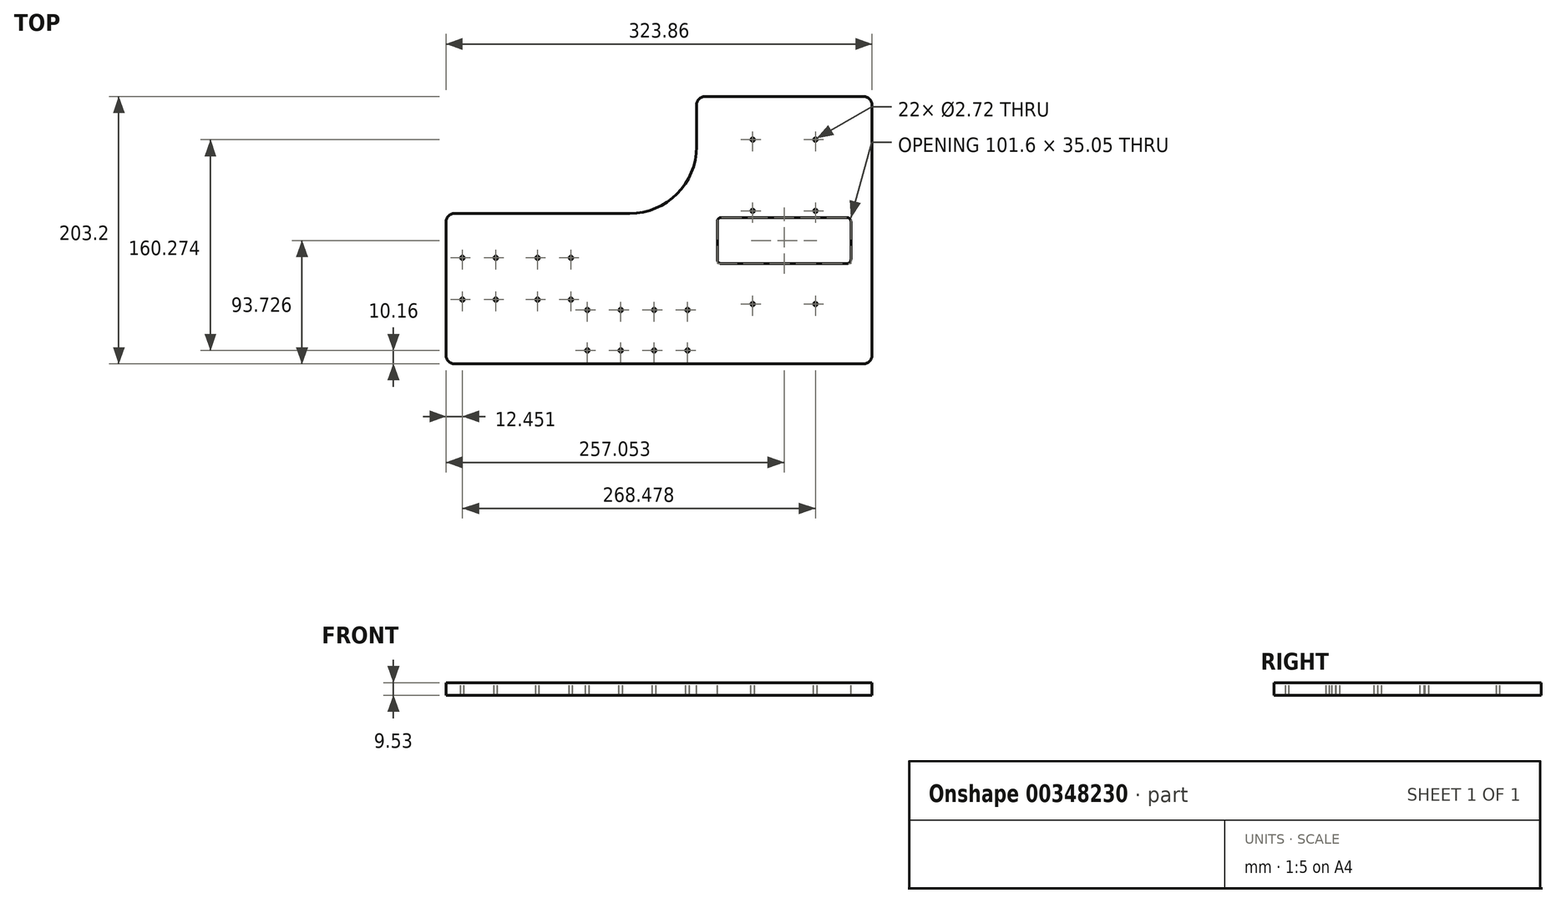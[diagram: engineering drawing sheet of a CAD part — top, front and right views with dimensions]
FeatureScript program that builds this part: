
annotation { "Feature Type Name" : "Feature", "Feature Type Description" : "" }
export const myFeature = defineFeature(function(context is Context, id is Id, definition is map)
    precondition{}
    {
        {
            var Q0;
            Q0=qCreatedBy(makeId("Top.planeOp"),FACE);
            var sketch = newSketch(context, id + "F0", { "sketchPlane" : qUnion([Q0])});
            skLineSegment(sketch, "E0", {"start": v(161.92, 95.25) * mm, "end": v(161.93, -95.25) * mm});
            skLineSegment(sketch, "E1", {"start": v(155.57, -101.6) * mm, "end": v(-155.58, -101.6) * mm});
            skLineSegment(sketch, "E2", {"start": v(-161.92, -95.25) * mm, "end": v(-161.92, 6.35) * mm});
            skLineSegment(sketch, "E3", {"start": v(-155.58, 12.7) * mm, "end": v(-22.22, 12.7) * mm});
            skLineSegment(sketch, "E4", {"start": v(28.58, 63.5) * mm, "end": v(28.58, 95.25) * mm});
            skLineSegment(sketch, "E5", {"start": v(34.93, 101.6) * mm, "end": v(155.57, 101.6) * mm});
            skPoint(sketch, "E6", {"position": v(0, -101.6) * mm});
            skPoint(sketch, "E7", {"position": v(161.92, 0) * mm});
            skPoint(sketch, "E8.visualSharp", {"position": v(28.58, 12.7) * mm});
            skArc(sketch, "E8.filletArc", {"start": v(-22.22, 12.7) * mm, "mid": v(13.7, 27.58) * mm, "end": v(28.58, 63.5) * mm});
            skPoint(sketch, "E9.visualSharp", {"position": v(161.93, -101.6) * mm});
            skArc(sketch, "E9.filletArc", {"start": v(155.57, -101.6) * mm, "mid": v(160.07, -99.74) * mm, "end": v(161.92, -95.25) * mm});
            skPoint(sketch, "E10.visualSharp", {"position": v(-161.92, -101.6) * mm});
            skArc(sketch, "E10.filletArc", {"start": v(-161.93, -95.25) * mm, "mid": v(-160.07, -99.74) * mm, "end": v(-155.58, -101.6) * mm});
            skPoint(sketch, "E11.visualSharp", {"position": v(-161.92, 12.7) * mm});
            skArc(sketch, "E11.filletArc", {"start": v(-155.58, 12.7) * mm, "mid": v(-160.07, 10.84) * mm, "end": v(-161.93, 6.35) * mm});
            skPoint(sketch, "E12.visualSharp", {"position": v(28.58, 101.6) * mm});
            skArc(sketch, "E12.filletArc", {"start": v(34.93, 101.6) * mm, "mid": v(30.43, 99.74) * mm, "end": v(28.58, 95.25) * mm});
            skPoint(sketch, "E13.visualSharp", {"position": v(161.92, 101.6) * mm});
            skArc(sketch, "E13.filletArc", {"start": v(161.92, 95.25) * mm, "mid": v(160.07, 99.74) * mm, "end": v(155.57, 101.6) * mm});
            skLineSegment(sketch, "E14.bottom", {"start": v(142.87, 9.65) * mm, "end": v(47.37, 9.65) * mm});
            skLineSegment(sketch, "E14.top", {"start": v(142.88, -25.4) * mm, "end": v(47.37, -25.4) * mm});
            skLineSegment(sketch, "E14.left", {"start": v(145.92, 6.6) * mm, "end": v(145.92, -22.35) * mm});
            skLineSegment(sketch, "E14.right", {"start": v(44.32, 6.6) * mm, "end": v(44.32, -22.35) * mm});
            skPoint(sketch, "E15.visualSharp", {"position": v(145.92, -25.4) * mm});
            skArc(sketch, "E15.filletArc", {"start": v(142.88, -25.4) * mm, "mid": v(145.03, -24.5) * mm, "end": v(145.92, -22.35) * mm});
            skPoint(sketch, "E16.visualSharp", {"position": v(44.32, -25.4) * mm});
            skArc(sketch, "E16.filletArc", {"start": v(44.32, -22.35) * mm, "mid": v(45.22, -24.5) * mm, "end": v(47.37, -25.4) * mm});
            skPoint(sketch, "E17.visualSharp", {"position": v(44.32, 9.65) * mm});
            skArc(sketch, "E17.filletArc", {"start": v(47.37, 9.65) * mm, "mid": v(45.22, 8.76) * mm, "end": v(44.32, 6.6) * mm});
            skPoint(sketch, "E18.visualSharp", {"position": v(145.92, 9.65) * mm});
            skArc(sketch, "E18.filletArc", {"start": v(145.92, 6.6) * mm, "mid": v(145.03, 8.76) * mm, "end": v(142.87, 9.65) * mm});
            skSolve(sketch);
        }
        {
            var Q0;
            Q0=qSketchRegion(id+"F0",true);
            extrude(context, id + "F1", {"entities" : qUnion([Q0]), "oppositeDirection" : true, "depth" : 9.52 * mm});
        }
        {
            var Q0;
            Q0=qCreatedBy(makeId("Top.planeOp"),FACE);
            var sketch = newSketch(context, id + "F2", { "sketchPlane" : qUnion([Q0])});
            skPoint(sketch, "E19", {"position": v(71.25, 68.83) * mm});
            skPoint(sketch, "E20", {"position": v(119, 68.83) * mm});
            skPoint(sketch, "E21", {"position": v(119, 14.73) * mm});
            skPoint(sketch, "E22", {"position": v(71.25, 14.73) * mm});
            skPoint(sketch, "E23", {"position": v(71.25, -56.13) * mm});
            skPoint(sketch, "E24", {"position": v(119, -56.13) * mm});
            skPoint(sketch, "E25", {"position": v(-149.48, -21.08) * mm});
            skPoint(sketch, "E26", {"position": v(-149.48, -52.83) * mm});
            skPoint(sketch, "E27", {"position": v(-124.08, -21.08) * mm});
            skPoint(sketch, "E28", {"position": v(-124.08, -52.83) * mm});
            skPoint(sketch, "E29", {"position": v(-92.33, -21.08) * mm});
            skPoint(sketch, "E30", {"position": v(-92.33, -52.83) * mm});
            skPoint(sketch, "E31", {"position": v(-66.93, -21.08) * mm});
            skPoint(sketch, "E32", {"position": v(-66.93, -52.83) * mm});
            skPoint(sketch, "E33", {"position": v(-54.48, -60.7) * mm});
            skPoint(sketch, "E34", {"position": v(-54.48, -91.44) * mm});
            skPoint(sketch, "E35", {"position": v(-29.08, -60.7) * mm});
            skPoint(sketch, "E36", {"position": v(-29.08, -91.44) * mm});
            skPoint(sketch, "E37", {"position": v(-3.68, -60.7) * mm});
            skPoint(sketch, "E38", {"position": v(-3.68, -91.44) * mm});
            skPoint(sketch, "E39", {"position": v(21.72, -60.7) * mm});
            skPoint(sketch, "E40", {"position": v(21.72, -91.44) * mm});
            skSolve(sketch);
        }
        {
            var Q0;
            Q0=sQuery(id+"F2.wireOp",VERTEX,"E24");
            var Q1;
            Q1=sQuery(id+"F2.wireOp",VERTEX,"E21");
            var Q2;
            Q2=sQuery(id+"F2.wireOp",VERTEX,"E20");
            var Q3;
            Q3=sQuery(id+"F2.wireOp",VERTEX,"E19");
            var Q4;
            Q4=sQuery(id+"F2.wireOp",VERTEX,"E22");
            var Q5;
            Q5=sQuery(id+"F2.wireOp",VERTEX,"E23");
            var Q6;
            Q6=sQuery(id+"F2.wireOp",VERTEX,"E39");
            var Q7;
            Q7=sQuery(id+"F2.wireOp",VERTEX,"E40");
            var Q8;
            Q8=sQuery(id+"F2.wireOp",VERTEX,"E37");
            var Q9;
            Q9=sQuery(id+"F2.wireOp",VERTEX,"E38");
            var Q10;
            Q10=sQuery(id+"F2.wireOp",VERTEX,"E35");
            var Q11;
            Q11=sQuery(id+"F2.wireOp",VERTEX,"E36");
            var Q12;
            Q12=sQuery(id+"F2.wireOp",VERTEX,"E34");
            var Q13;
            Q13=sQuery(id+"F2.wireOp",VERTEX,"E33");
            var Q14;
            Q14=sQuery(id+"F2.wireOp",VERTEX,"E32");
            var Q15;
            Q15=sQuery(id+"F2.wireOp",VERTEX,"E31");
            var Q16;
            Q16=sQuery(id+"F2.wireOp",VERTEX,"E30");
            var Q17;
            Q17=sQuery(id+"F2.wireOp",VERTEX,"E29");
            var Q18;
            Q18=sQuery(id+"F2.wireOp",VERTEX,"E28");
            var Q19;
            Q19=sQuery(id+"F2.wireOp",VERTEX,"E27");
            var Q20;
            Q20=sQuery(id+"F2.wireOp",VERTEX,"E26");
            var Q21;
            Q21=sQuery(id+"F2.wireOp",VERTEX,"E25");
            var Q22;
            Q22=makeQuery(id+"F1.opExtrude","SWEPT_BODY",BODY,{"disambiguationData":[OSD([sQuery(id+"F0.wireOp",EDGE,"E0"),sQuery(id+"F0.wireOp",EDGE,"E1"),sQuery(id+"F0.wireOp",EDGE,"E2"),sQuery(id+"F0.wireOp",EDGE,"E3"),sQuery(id+"F0.wireOp",EDGE,"E4"),sQuery(id+"F0.wireOp",EDGE,"E5"),sQuery(id+"F0.wireOp",EDGE,"E8.filletArc"),sQuery(id+"F0.wireOp",EDGE,"E9.filletArc"),sQuery(id+"F0.wireOp",EDGE,"E10.filletArc"),sQuery(id+"F0.wireOp",EDGE,"E11.filletArc"),sQuery(id+"F0.wireOp",EDGE,"E12.filletArc"),sQuery(id+"F0.wireOp",EDGE,"E13.filletArc"),sQuery(id+"F0.wireOp",EDGE,"E14.bottom"),sQuery(id+"F0.wireOp",EDGE,"E14.top"),sQuery(id+"F0.wireOp",EDGE,"E14.left"),sQuery(id+"F0.wireOp",EDGE,"E14.right"),sQuery(id+"F0.wireOp",EDGE,"E15.filletArc"),sQuery(id+"F0.wireOp",EDGE,"E16.filletArc"),sQuery(id+"F0.wireOp",EDGE,"E17.filletArc"),sQuery(id+"F0.wireOp",EDGE,"E18.filletArc")])]});
            hole(context, id + "F3", {"style" : HoleStyle.SIMPLE, "holeDiameter" : 2.72 * mm, "endStyle" : HoleEndStyle.THROUGH, "locations" : qUnion([Q0, Q1, Q2, Q3, Q4, Q5, Q6, Q7, Q8, Q9, Q10, Q11, Q12, Q13, Q14, Q15, Q16, Q17, Q18, Q19, Q20, Q21]), "scope" : qUnion([Q22])});
        }
    });
